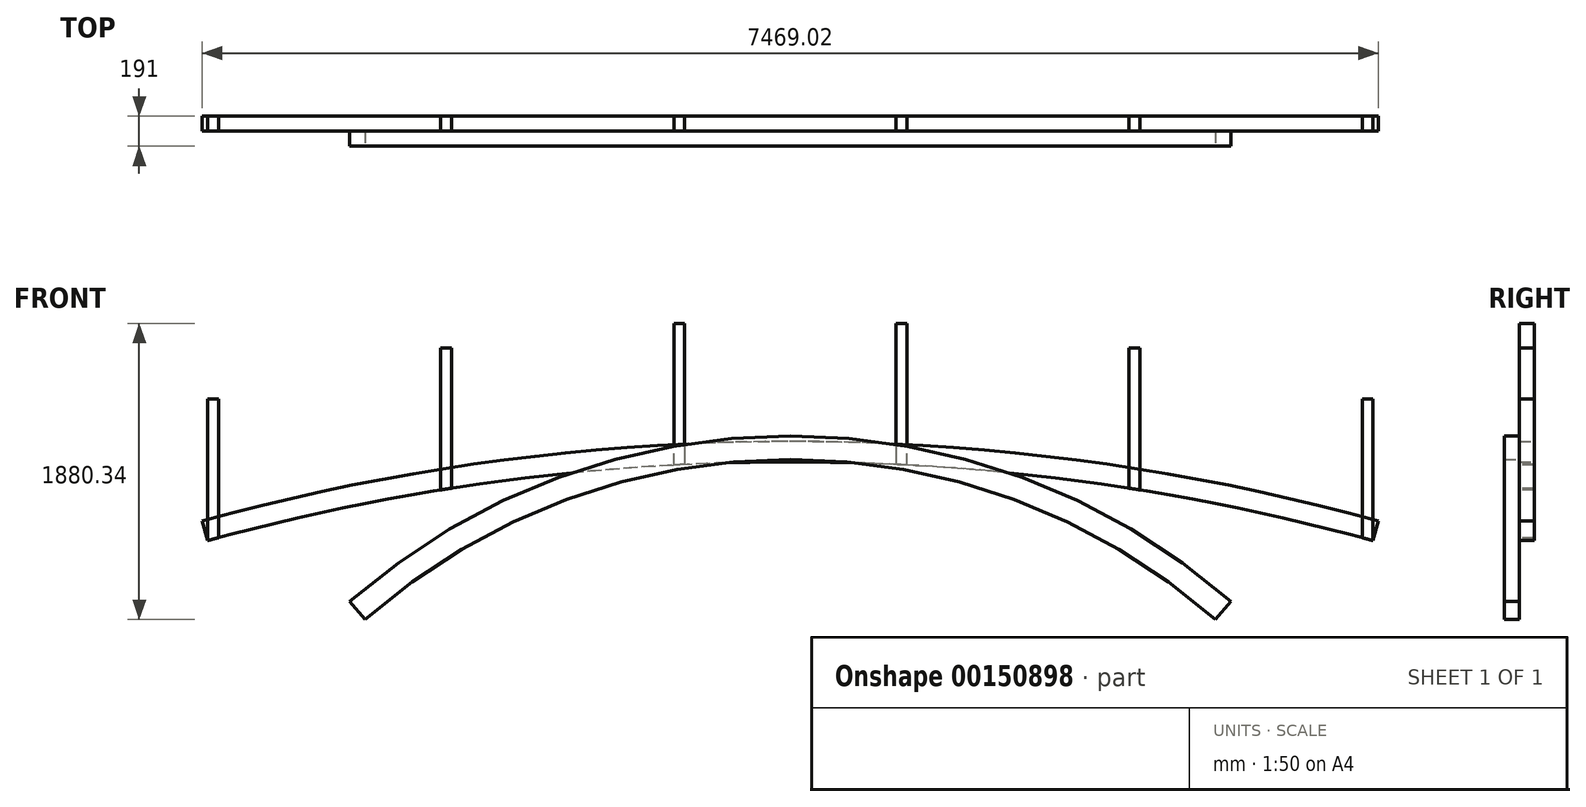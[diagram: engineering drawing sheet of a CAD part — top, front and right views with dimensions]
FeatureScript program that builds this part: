
annotation { "Feature Type Name" : "Feature", "Feature Type Description" : "" }
export const myFeature = defineFeature(function(context is Context, id is Id, definition is map)
    precondition{}
    {
        {
            var Q0;
            Q0=qCreatedBy(makeId("Front.planeOp"),FACE);
            var sketch = newSketch(context, id + "F0", { "sketchPlane" : qUnion([Q0])});
            skArc(sketch, "E0", {"start": v(3028, 0) * mm, "mid": v(-672, 500) * mm, "end": v(-4372, 0) * mm});
            skLineSegment(sketch, "E1", {"start": v(-4372, 0) * mm, "end": v(3028, 0) * mm});
            skLineSegment(sketch, "E2", {"start": v(-672, 0) * mm, "end": v(-672, 500) * mm});
            skLineSegment(sketch, "E3", {"start": v(-672, 0) * mm, "end": v(-672, -500) * mm});
            skLineSegment(sketch, "E4", {"start": v(-3372, -500) * mm, "end": v(2028, -500) * mm});
            skArc(sketch, "E5", {"start": v(2028, -500) * mm, "mid": v(-672, 514.55) * mm, "end": v(-3372, -500) * mm});
            skLineSegment(sketch, "E6", {"start": v(-3372, -500) * mm, "end": v(-4545, -1526.46) * mm});
            skLineSegment(sketch, "E7", {"start": v(-3372, -500) * mm, "end": v(-3470.78, -387.12) * mm});
            skLineSegment(sketch, "E8", {"start": v(-4372, 0) * mm, "end": v(-4716.8, -94.92) * mm});
            skLineSegment(sketch, "E9", {"start": v(-4372, 0) * mm, "end": v(-4406.5, 125.34) * mm});
            skLineSegment(sketch, "E10", {"start": v(-4372, 0) * mm, "end": v(-4372, 900) * mm});
            skLineSegment(sketch, "E11", {"start": v(-2892, 322.1) * mm, "end": v(-2892, 1222.1) * mm});
            skLineSegment(sketch, "E12", {"start": v(-1412, 480.34) * mm, "end": v(-1412, 1380.34) * mm});
            skLineSegment(sketch, "E13", {"start": v(68, 480.34) * mm, "end": v(68, 1380.34) * mm});
            skLineSegment(sketch, "E14", {"start": v(3028, 0) * mm, "end": v(3028, 900) * mm});
            skLineSegment(sketch, "E15", {"start": v(1548, 322.1) * mm, "end": v(1548, 1222.1) * mm});
            skLineSegment(sketch, "E16", {"start": v(-4372, 900) * mm, "end": v(-4304, 900) * mm});
            skLineSegment(sketch, "E17", {"start": v(-4304, 900) * mm, "end": v(-4304, 18.54) * mm});
            skLineSegment(sketch, "E18", {"start": v(-2892, 1222.1) * mm, "end": v(-2824, 1222.1) * mm});
            skLineSegment(sketch, "E19", {"start": v(-2824, 1222.1) * mm, "end": v(-2824, 332.89) * mm});
            skLineSegment(sketch, "E20", {"start": v(-1412, 1380.34) * mm, "end": v(-1344, 1380.34) * mm});
            skLineSegment(sketch, "E21", {"start": v(-1344, 1380.34) * mm, "end": v(-1344, 483.8) * mm});
            skLineSegment(sketch, "E22", {"start": v(68, 1380.34) * mm, "end": v(0, 1380.34) * mm});
            skLineSegment(sketch, "E23", {"start": v(0, 1380.34) * mm, "end": v(0, 483.8) * mm});
            skLineSegment(sketch, "E24", {"start": v(1548, 1222.1) * mm, "end": v(1480, 1222.1) * mm});
            skLineSegment(sketch, "E25", {"start": v(1480, 1222.1) * mm, "end": v(1480, 332.89) * mm});
            skLineSegment(sketch, "E26", {"start": v(3028, 900) * mm, "end": v(2960, 900) * mm});
            skLineSegment(sketch, "E27", {"start": v(2960, 900) * mm, "end": v(2960, 18.54) * mm});
            skSolve(sketch);
        }
        {
            var Q0;
            Q0=sQuery(id+"F0.wireOp",EDGE,"E7");
            extrude(context, id + "F1", {"bodyType" : ExtendedToolBodyType.SURFACE, "surfaceEntities" : qUnion([Q0]), "depth" : 95 * mm});
        }
        {
            var Q0;
            Q0=makeQuery(id+"F1.opExtrude","SWEPT_FACE",FACE,{"disambiguationData":[OSD([sQuery(id+"F0.wireOp",EDGE,"E7")])]});
            var Q1;
            Q1=sQuery(id+"F0.wireOp",EDGE,"E5");
            sweep(context, id + "F2", {"profiles" : qUnion([Q0]), "path" : qUnion([Q1])});
        }
        {
            var Q0;
            Q0=sQuery(id+"F0.wireOp",EDGE,"E9");
            extrude(context, id + "F3", {"bodyType" : ExtendedToolBodyType.SURFACE, "surfaceEntities" : qUnion([Q0]), "depth" : 96 * mm});
        }
        {
            var Q0;
            Q0=makeQuery(id+"F3.opExtrude","SWEPT_FACE",FACE,{"disambiguationData":[OSD([sQuery(id+"F0.wireOp",EDGE,"E9")])]});
            var Q1;
            Q1=sQuery(id+"F0.wireOp",EDGE,"E0");
            sweep(context, id + "F4", {"profiles" : qUnion([Q0]), "path" : qUnion([Q1])});
        }
        {
            var Q0;
            Q0=makeQuery(id+"F4.opSweep","SWEPT_BODY",BODY,{"disambiguationData":[OSD([sQuery(id+"F0.wireOp",EDGE,"E0"),sQuery(id+"F0.wireOp",EDGE,"E9")])]});
            transform(context, id + "F5", {"entities" : qUnion([Q0]), "transformType" : TransformType.TRANSLATION_3D, "dx" : 0 * mm, "dy" : 96 * mm, "dz" : 0 * mm, "makeCopy" : false});
        }
        {
            var Q0;
            {var subQ0=sQuery(id+"F0.wireOp",EDGE,"E10");Q0=makeQuery(id+"F0.imprint","IMPRINT",FACE,{"disambiguationData":[TD([[makeQuery(id+"F0.imprint","IMPRINT",EDGE,{"derivedFrom":subQ0}),-1.0]])]});}
            var Q1;
            {var subQ0=sQuery(id+"F0.wireOp",EDGE,"E11");Q1=makeQuery(id+"F0.imprint","IMPRINT",FACE,{"disambiguationData":[TD([[makeQuery(id+"F0.imprint","IMPRINT",EDGE,{"derivedFrom":subQ0}),-1.0]])]});}
            var Q2;
            {var subQ0=sQuery(id+"F0.wireOp",EDGE,"E12");var subQ1=sQuery(id+"F0.wireOp",EDGE,"E0");var subQ2=makeQuery(id+"F0.imprint","INTERSECT",VERTEX,{"derivedFrom":[subQ1,subQ0]});Q2=makeQuery(id+"F0.imprint","IMPRINT",FACE,{"disambiguationData":[TD([[makeQuery(id+"F0.imprint","IMPRINT",EDGE,{"disambiguationData":[TD([[subQ2,1.0]])],"derivedFrom":subQ1}),-1.0]])]});}
            var Q3;
            {var subQ5=sQuery(id+"F0.wireOp",EDGE,"E20");Q3=makeQuery(id+"F0.imprint","IMPRINT",FACE,{"disambiguationData":[TD([[makeQuery(id+"F0.imprint","IMPRINT",EDGE,{"derivedFrom":subQ5}),-1.0]])]});}
            var Q4;
            {var subQ5=sQuery(id+"F0.wireOp",EDGE,"E22");Q4=makeQuery(id+"F0.imprint","IMPRINT",FACE,{"disambiguationData":[TD([[makeQuery(id+"F0.imprint","IMPRINT",EDGE,{"derivedFrom":subQ5}),1.0]])]});}
            var Q5;
            {var subQ0=sQuery(id+"F0.wireOp",EDGE,"E13");var subQ1=sQuery(id+"F0.wireOp",EDGE,"E0");var subQ2=makeQuery(id+"F0.imprint","INTERSECT",VERTEX,{"derivedFrom":[subQ1,subQ0]});Q5=makeQuery(id+"F0.imprint","IMPRINT",FACE,{"disambiguationData":[TD([[makeQuery(id+"F0.imprint","IMPRINT",EDGE,{"disambiguationData":[TD([[subQ2,-1.0]])],"derivedFrom":subQ1}),-1.0]])]});}
            var Q6;
            {var subQ0=sQuery(id+"F0.wireOp",EDGE,"E15");Q6=makeQuery(id+"F0.imprint","IMPRINT",FACE,{"disambiguationData":[TD([[makeQuery(id+"F0.imprint","IMPRINT",EDGE,{"derivedFrom":subQ0}),1.0]])]});}
            var Q7;
            {var subQ0=sQuery(id+"F0.wireOp",EDGE,"E14");Q7=makeQuery(id+"F0.imprint","IMPRINT",FACE,{"disambiguationData":[TD([[makeQuery(id+"F0.imprint","IMPRINT",EDGE,{"derivedFrom":subQ0}),1.0]])]});}
            extrude(context, id + "F6", {"entities" : qUnion([Q0, Q1, Q2, Q3, Q4, Q5, Q6, Q7]), "oppositeDirection" : true, "depth" : 96 * mm});
        }
    });
